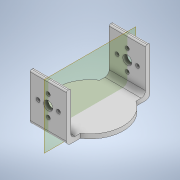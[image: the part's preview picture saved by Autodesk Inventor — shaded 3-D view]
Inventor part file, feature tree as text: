
AUTODESK INVENTOR PART (.ipt)
format: ipt  version: 2022 (Build 260153000, 153)  size: 466,944 bytes
history: native  units: mm
features: fillet x8, sketch x8, extrude x7, other x3, pattern_circular x1, mirror x1, revolve x1, projected_geometry x1
ambient origin geometry x8: Origin, YZ Plane, XZ Plane, XY Plane, X Axis, Y Axis, Z Axis, Center Point
bodies: Body1 (feature_tree)
feature tree (30):
  other  "Твердое тело1"
  extrude  "Выдавливание1"  Depth=51.5mm
  extrude  "Выдавливание2"  Depth=25.0mm
  fillet  "Сопряжение1"  Radius=45.8mm
  extrude  "Выдавливание3"  Depth=3.0mm TaperAngle=0.0deg
  extrude  "Выдавливание4"  Depth=37.8mm
  fillet  "Сопряжение4"  Radius=2.0mm
  fillet  "Сопряжение10"  Radius=1.0mm
  pattern_circular  "Круговой массив1"  [2 undecoded]
  fillet  "Сопряжение5"  Radius=24.7mm
  other  "РабПлоскость1"
  extrude  "Выдавливание5"  Depth=7.0mm TaperAngle=0.0deg
  fillet  "Сопряжение6"  Radius=10.0mm
  fillet  "Сопряжение7"  Radius=0.7mm
  mirror  "Зеркальное отражение1"
  fillet  "Сопряжение8"  Radius=80.0mm
  extrude  "Выдавливание6"  Depth=0.2mm
  extrude  "Выдавливание7"  Depth=30.0mm
  fillet  "Сопряжение9"  Radius=6.2mm
  other  "РабПлоскость2"
  revolve  "Вращение1"
  sketch  "Эскиз1"
  sketch  "Эскиз2"
  sketch  "Эскиз3"
  sketch  "Эскиз4"
  sketch  "Эскиз6"
  sketch  "Эскиз7"
  sketch  "Эскиз8"
  sketch  "Эскиз9"
  projected_geometry  "Спроецированная петля1"
note: 2 required parameter values undecoded (feature->parameter linkage not recoverable at this tier; creation-order binding heuristic only, values carry confidence <= 0.55)
